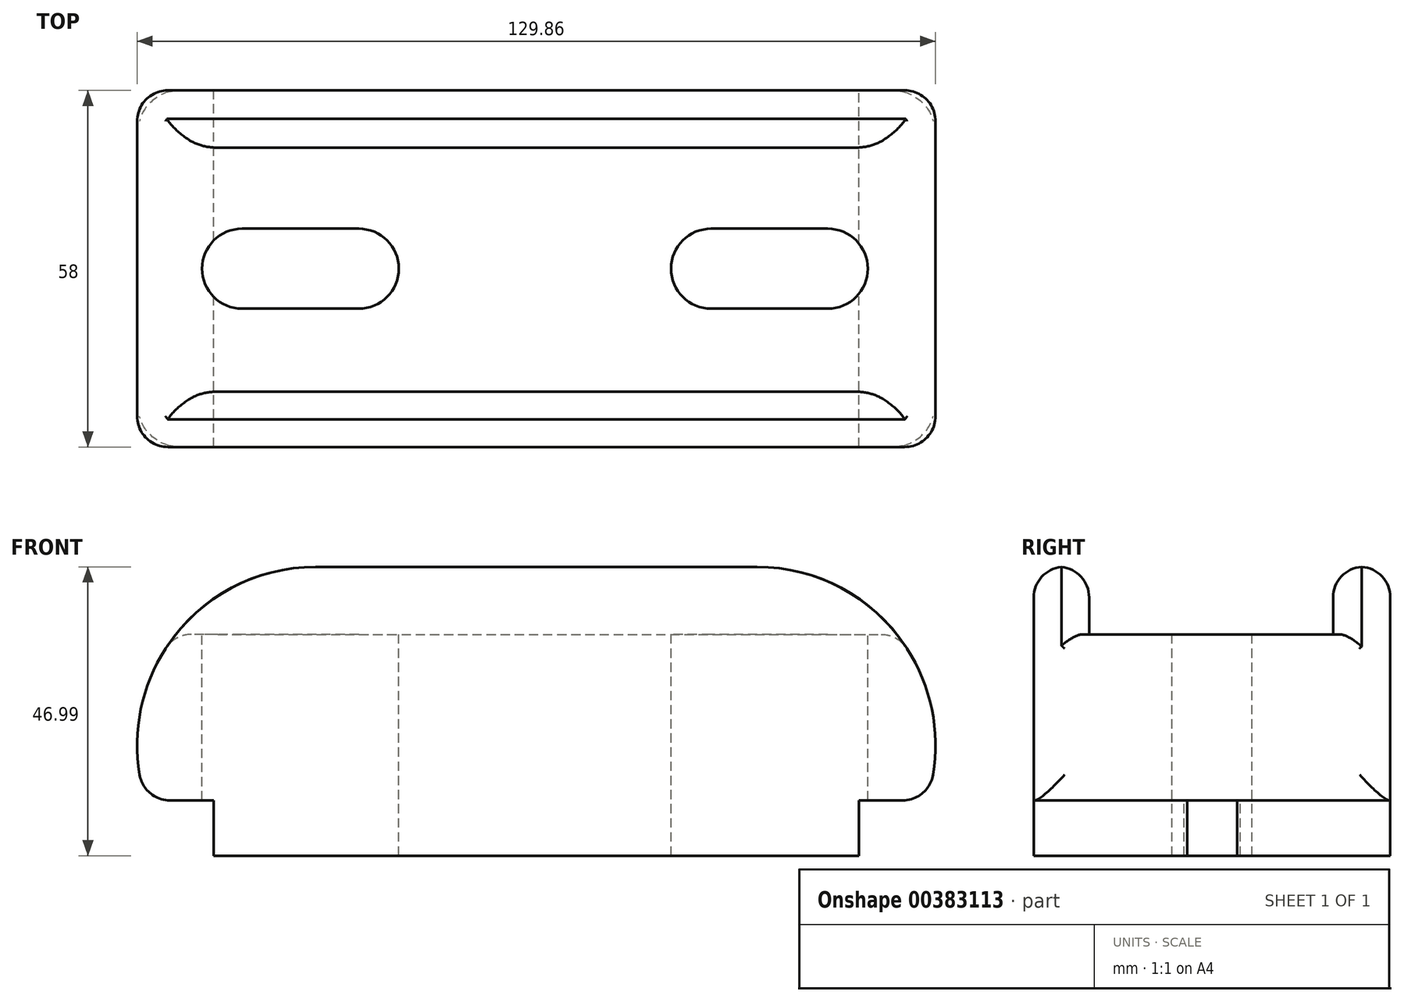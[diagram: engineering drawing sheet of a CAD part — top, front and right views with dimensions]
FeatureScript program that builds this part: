
annotation { "Feature Type Name" : "Feature", "Feature Type Description" : "" }
export const myFeature = defineFeature(function(context is Context, id is Id, definition is map)
    precondition{}
    {
        {
            var Q0;
            Q0=qCreatedBy(makeId("Front.planeOp"),FACE);
            var sketch = newSketch(context, id + "F0", { "sketchPlane" : qUnion([Q0])});
            skLineSegment(sketch, "E0", {"start": v(-52.5, 0) * mm, "end": v(52.5, 0) * mm});
            skLineSegment(sketch, "E1", {"start": v(52.5, 0) * mm, "end": v(52.5, 9) * mm});
            skLineSegment(sketch, "E2", {"start": v(52.5, 9) * mm, "end": v(63.5, 9) * mm});
            skArc(sketch, "E3", {"start": v(63.5, 9) * mm, "mid": v(59.4, 35.03) * mm, "end": v(35.93, 47) * mm});
            skLineSegment(sketch, "E4", {"start": v(-52.5, 0) * mm, "end": v(-52.5, 9) * mm});
            skLineSegment(sketch, "E5", {"start": v(-52.5, 9) * mm, "end": v(-63.5, 9) * mm});
            skArc(sketch, "E6", {"start": v(-35.93, 47) * mm, "mid": v(-59.4, 35.03) * mm, "end": v(-63.5, 9) * mm});
            skLineSegment(sketch, "E7", {"start": v(-35.93, 47) * mm, "end": v(35.93, 47) * mm});
            skLineSegment(sketch, "E8", {"start": v(0, 74.35) * mm, "end": v(0, 0) * mm, "construction": true});
            skSolve(sketch);
        }
        {
            var Q0;
            Q0=makeQuery(id+"F0.imprint","IMPRINT",FACE,{"disambiguationData":[TD([[makeQuery(id+"F0.imprint","IMPRINT",EDGE,{"derivedFrom":sQuery(id+"F0.wireOp",EDGE,"E0")}),1.0]])]});
            extrude(context, id + "F1", {"entities" : qUnion([Q0]), "endBound" : BoundingType.SYMMETRIC, "depth" : 58 * mm});
        }
        {
            var Q0;
            Q0=qCreatedBy(makeId("Right.planeOp"),FACE);
            var sketch = newSketch(context, id + "F2", { "sketchPlane" : qUnion([Q0])});
            skLineSegment(sketch, "E9.bottom", {"start": v(19.69, 47) * mm, "end": v(-20, 47) * mm});
            skLineSegment(sketch, "E9.top", {"start": v(19.69, 36) * mm, "end": v(-20, 36) * mm});
            skLineSegment(sketch, "E9.left", {"start": v(19.69, 47) * mm, "end": v(19.69, 36) * mm});
            skLineSegment(sketch, "E9.right", {"start": v(-20, 47) * mm, "end": v(-20, 36) * mm});
            skSolve(sketch);
        }
        {
            var Q0;
            Q0=makeQuery(id+"F2.imprint","IMPRINT",FACE,{"disambiguationData":[TD([[makeQuery(id+"F2.imprint","IMPRINT",EDGE,{"derivedFrom":sQuery(id+"F2.wireOp",EDGE,"E9.bottom")}),1.0]])]});
            extrude(context, id + "F3", {"entities" : qUnion([Q0]), "operationType" : NewBodyOperationType.REMOVE, "endBound" : BoundingType.THROUGH_ALL, "oppositeDirection" : true, "depth" : 25 * mm, "hasSecondDirection" : true, "secondDirectionOppositeDirection" : false, "secondDirectionDepth" : 94 * mm});
        }
        {
            var Q0;
            Q0=makeQuery(id+"F3.boolean.opBoolean","COPY",FACE,{"derivedFrom":makeQuery(id+"F3.opExtrude","SWEPT_FACE",FACE,{"disambiguationData":[OSD([sQuery(id+"F2.wireOp",EDGE,"E9.top")])]})});
            var sketch = newSketch(context, id + "F4", { "sketchPlane" : qUnion([Q0])});
            skArc(sketch, "E10", {"start": v(47.43, -6.5) * mm, "mid": v(53.93, 0) * mm, "end": v(47.43, 6.5) * mm});
            skArc(sketch, "E11", {"start": v(28.43, 6.5) * mm, "mid": v(21.93, 0) * mm, "end": v(28.43, -6.5) * mm});
            skArc(sketch, "E12", {"start": v(-28.88, -6.5) * mm, "mid": v(-22.38, 0) * mm, "end": v(-28.88, 6.5) * mm});
            skArc(sketch, "E13", {"start": v(-47.88, 6.5) * mm, "mid": v(-54.38, 0) * mm, "end": v(-47.88, -6.5) * mm});
            skLineSegment(sketch, "E14", {"start": v(47.43, -6.5) * mm, "end": v(28.43, -6.5) * mm});
            skLineSegment(sketch, "E15", {"start": v(47.43, 6.5) * mm, "end": v(28.43, 6.5) * mm});
            skLineSegment(sketch, "E16", {"start": v(-28.88, -6.5) * mm, "end": v(-47.88, -6.5) * mm});
            skLineSegment(sketch, "E17", {"start": v(-28.88, 6.5) * mm, "end": v(-47.88, 6.5) * mm});
            skSolve(sketch);
        }
        {
            var Q0;
            Q0=makeQuery(id+"F4.imprint","IMPRINT",FACE,{"disambiguationData":[TD([[makeQuery(id+"F4.imprint","IMPRINT",EDGE,{"derivedFrom":sQuery(id+"F4.wireOp",EDGE,"E12")}),1.0]])]});
            var Q1;
            Q1=makeQuery(id+"F4.imprint","IMPRINT",FACE,{"disambiguationData":[TD([[makeQuery(id+"F4.imprint","IMPRINT",EDGE,{"derivedFrom":sQuery(id+"F4.wireOp",EDGE,"E10")}),1.0]])]});
            extrude(context, id + "F5", {"entities" : qUnion([Q0, Q1]), "operationType" : NewBodyOperationType.REMOVE, "endBound" : BoundingType.THROUGH_ALL, "oppositeDirection" : true, "depth" : 25 * mm});
        }
        {
            var Q0;
            {var subQ0=sQuery(id+"F0.wireOp",EDGE,"E7");Q0=makeQuery(id+"F3.boolean.opBoolean","SPLIT",FACE,{"disambiguationData":[TD([makeQuery(id+"F3.opExtrude","SWEPT_FACE",FACE,{"disambiguationData":[OSD([sQuery(id+"F2.wireOp",EDGE,"E9.left")])]})])],"derivedFrom":makeQuery(id+"F1.opExtrude","SWEPT_FACE",FACE,{"disambiguationData":[OSD([subQ0])]})});}
            var Q1;
            Q1=makeQuery(id+"F1.opExtrude","SWEPT_FACE",FACE,{"disambiguationData":[OSD([sQuery(id+"F0.wireOp",EDGE,"E6")])]});
            var Q2;
            Q2=makeQuery(id+"F1.opExtrude","SWEPT_FACE",FACE,{"disambiguationData":[OSD([sQuery(id+"F0.wireOp",EDGE,"E3")])]});
            fillet(context, id + "F6", {"entities" : qUnion([Q0, Q1, Q2]), "radius" : 5 * mm, "tangentPropagation" : true, "allowEdgeOverflow" : false});
        }
    });
